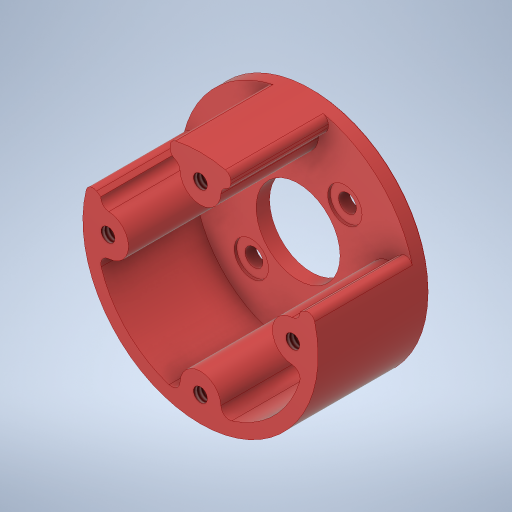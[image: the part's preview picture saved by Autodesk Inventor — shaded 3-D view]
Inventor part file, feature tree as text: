
AUTODESK INVENTOR PART (.ipt)
format: ipt  version: 2023 (Build 270158000, 158)  size: 398,848 bytes
history: native  units: in
note: dims shown in document units (in); Inventor stores cm internally (conversion verified against a paired STEP export)
features: sketch x4, extrude x3, hole x2, fillet x2, shell x1, chamfer x1
ambient origin geometry x8: Origin, YZ Plane, XZ Plane, XY Plane, X Axis, Y Axis, Z Axis, Center Point
bodies: Solid1 (feature_tree)
feature tree (13):
  extrude  "Extrusion1"  Depth=0.8268in TaperAngle=0.0deg
  hole  "Hole1"  [1 undecoded]
  shell  "Shell1"  Thickness=0.0625in
  fillet  "Fillet1"  Radius=0.45in
  extrude  "Extrusion2"  Depth=0.05in
  fillet  "Fillet2"  Radius=0.625in
  extrude  "Extrusion3"  TaperAngle=0.0deg  [1 undecoded]
  chamfer  "Chamfer1"  Distance=0.0079in Angle=45.0deg
  hole  "Hole2"  [1 undecoded]
  sketch  "Sketch1"  dims[d0=1.75in d1=0.8268in d2=0.0in]
  sketch  "Sketch2"  dims[d4=1.5748in d6=360.0deg]
  sketch  "Sketch3"  dims[d8=0.104in d9=0.276in d10=0.248in d11=0.25in d12=90.0deg d13=1.0in d14=0.8108in d15=0.1in d16=0.0625in d17=0.45in]
  sketch  "Sketch4"  dims[d18=0.7874in d19=0.0in d20=0.05in d21=0.625in d22=0.0in d23=0.0in d24=0.0079in d25=0.125in d26=45.0deg d27=45.0deg d28=1.5748in d30=360.0deg d32=0.134in d33=0.276in d34=0.256in d35=0.0197in d36=90.0deg d37=1.0in d38=0.8108in d39=0.9843in d40=0.1875in]
note: 3 required parameter values undecoded (feature->parameter linkage not recoverable at this tier; creation-order binding heuristic only, values carry confidence <= 0.55)
